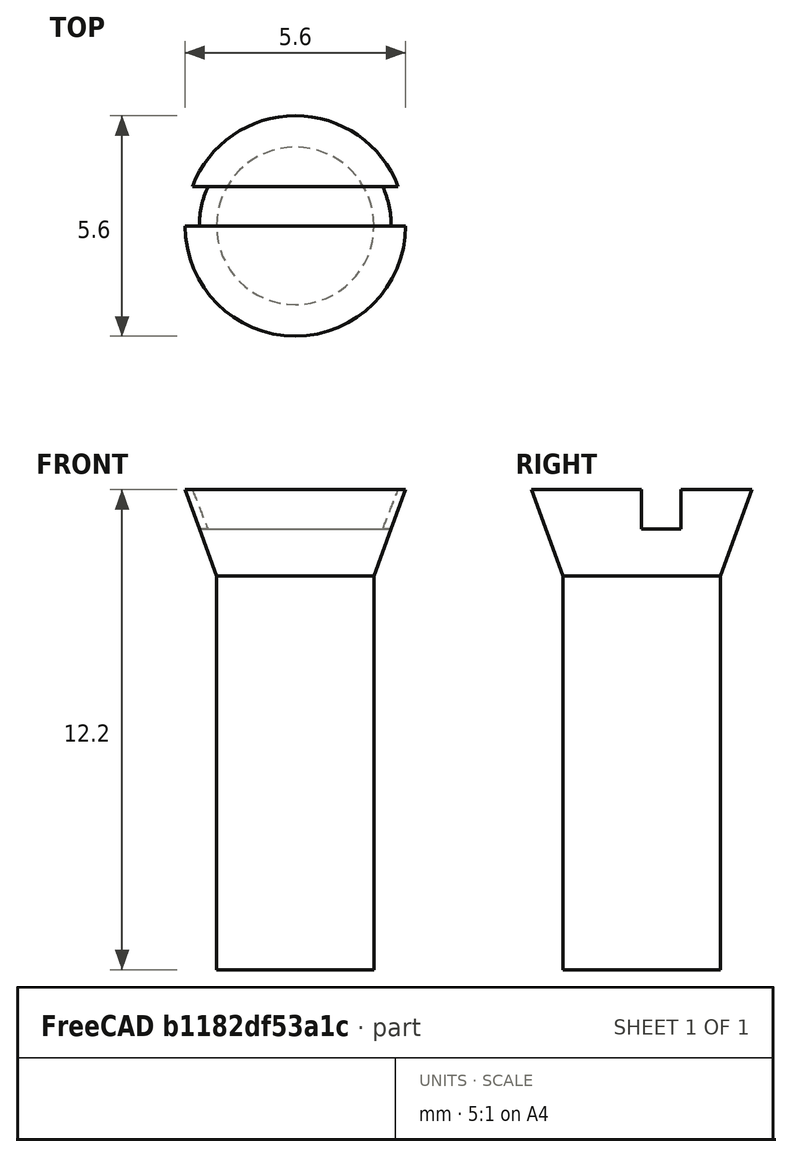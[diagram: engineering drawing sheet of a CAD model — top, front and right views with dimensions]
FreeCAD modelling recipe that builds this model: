
FCSTD DOCUMENT  (FreeCAD 0.21R33694 (Git))
Label: OJT1_T14R01_tornillo
License: All rights reserved
LicenseURL: http://en.wikipedia.org/wiki/All_rights_reserved
objects: Part::Cone×1, Part::Cylinder×1, Part::Box×1, Part::Cut×1, Part::Fuse×1
note: 5 computed .brp shape members not serialized (recipe doc carries the construction recipe); baked Part::Feature solids carry a one-line shape summary decoded from their .brp

FEATURE [Part::Cone] Cone  label="primera_part"
  Angle = 360
  AttacherType = Attacher::AttachEngine3D
  Height = 2.2
  Placement = pos=(0,0,10) rot=(0,0,1;0rad)
  Radius1 = 2
  Radius2 = 2.8
FEATURE [Part::Cylinder] Cylinder
  Angle = 360
  AttacherType = Attacher::AttachEngine3D
  FirstAngle = 0
  Height = 10
  Radius = 2
  SecondAngle = 0
FEATURE [Part::Box] Box  label="Cube"
  AttacherType = Attacher::AttachEngine3D
  Height = 2
  Length = 10
  Placement = pos=(-5,0,11.2) rot=(0,0,1;0rad)
  Width = 1
FEATURE [Part::Cut] Cut
  Base = -> Cone
  Refine = true
  Tool = -> Box
FEATURE [Part::Fuse] Fusion
  Base = -> Cylinder
  Refine = true
  Tool = -> Cut
